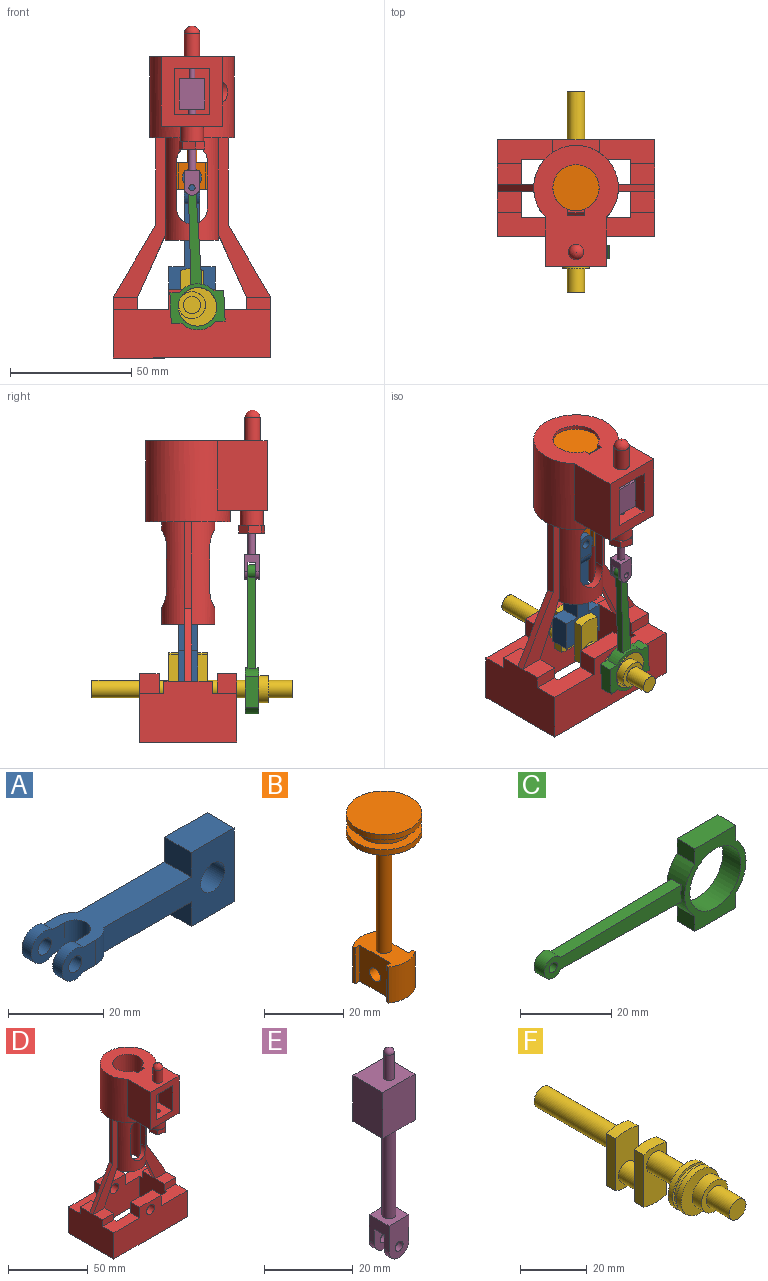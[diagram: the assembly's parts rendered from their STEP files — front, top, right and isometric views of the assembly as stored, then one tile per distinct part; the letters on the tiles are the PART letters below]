
ASSEMBLY  parts=6 mates=7
PART A: 21 faces, bbox 53.2x11.9x19.1 mm
  f0: plane 12.7x7.94mm, normal (0,0,1), area 100.8mm2, adj f1,f2,f13,f15
  f1: plane 19.05x7.94mm, normal (1,0,0), area 151.2mm2, adj f0,f8,f13,f15
  f2: plane 7.94x6.35mm, normal (-1,0,0), area 50.4mm2, adj f0,f3,f13,f15
  f3: plane 34.13x11.91mm, normal (0,0,1), area 258.6mm2, adj f2,f4,f5,f10,f11,f13,f14,f15
  f4: cylinder r=3.97mm len=7.94mm, axis (0,-1,0), area 48.8mm2, adj f3,f6,f11,f18
  f5: cylinder r=3.97mm len=7.94mm, axis (0,-1,0), area 48.8mm2, adj f3,f6,f10,f19
  f6: plane 34.13x11.91mm, normal (0,0,-1), area 258.6mm2, adj f4,f5,f7,f10,f11,f13,f14,f15
  f7: plane 7.94x6.35mm, normal (-1,0,0), area 50.4mm2, adj f6,f8,f13,f15
  f8: plane 12.7x7.94mm, normal (0,0,-1), area 100.8mm2, adj f1,f7,f13,f15
  f9: cylinder r=1.98mm len=3.97mm, axis (0,-1,0), area 34.6mm2, adj f11,f18
  f10: plane 10x7.94mm, normal (0,1,0), area 53.2mm2, adj f3,f5,f6,f12,f16
  f11: plane 10x7.94mm, normal (0,-1,0), area 53.2mm2, adj f3,f4,f6,f9,f14
  f12: cylinder r=1.98mm len=3.97mm, axis (0,-1,0), area 34.6mm2, adj f10,f19
  f13: plane 38.74x19.05mm, normal (0,-1,0), area 367.2mm2, adj f0,f1,f2,f3,f6,f7,f8,f14
  f14: cylinder r=5.95mm len=6.35mm, axis (0,0,1), area 31.8mm2, adj f3,f6,f11,f13
  f15: plane 38.74x19.05mm, normal (0,1,0), area 367.2mm2, adj f0,f1,f2,f3,f6,f7,f8,f16
  f16: cylinder r=5.95mm len=6.35mm, axis (0,0,1), area 31.8mm2, adj f3,f6,f10,f15
  f17: cylinder r=3.17mm len=6.35mm, axis (0,0,1), area 63.3mm2, adj f3,f6,f18,f19
  f18: plane 10x7.94mm, normal (0,1,0), area 53.2mm2, adj f3,f4,f6,f9,f17
  f19: plane 10x7.94mm, normal (0,-1,0), area 53.2mm2, adj f3,f5,f6,f12,f17
  f20: cylinder r=3.57mm len=7.94mm, axis (0,-1,0), area 178.1mm2, adj f13,f15
PART B: 23 faces, bbox 19.1x19.1x53.2 mm
  f0: cylinder r=9.53mm len=19.05mm, axis (0,0,1), area 100.2mm2, adj f1,f7
  f1: plane 19.05x19.05mm, normal (0,0,1), area 285mm2, adj f0
  f2: cylinder r=1.98mm len=35.72mm, axis (0,0,1), area 445.3mm2, adj f3,f21
  f3: plane 19.05x19.05mm, normal (0,0,-1), area 272.7mm2, adj f2,f4
  f4: cylinder r=9.53mm len=19.05mm, axis (0,0,1), area 100.2mm2, adj f3,f5
  f5: plane 19.05x19.05mm, normal (0,0,1), area 131.1mm2, adj f4,f6
  f6: cylinder r=7mm len=14mm, axis (0,0,1), area 131.9mm2, adj f5,f7
  f7: plane 19.05x19.05mm, normal (0,0,-1), area 131.1mm2, adj f0,f6
  f8: plane 11.11x0.85mm, normal (-1,0,0), area 9.4mm2, adj f9,f19,f20,f21
  f9: cylinder r=7.94mm len=11.11mm, axis (0,0,1), area 113.5mm2, adj f8,f10,f20,f21
  f10: plane 11.11x0.85mm, normal (1,0,0), area 9.4mm2, adj f9,f11,f20,f21
  f11: plane 11.11x1.59mm, normal (0,-1,0), area 17.6mm2, adj f10,f12,f20,f21
  f12: plane 11.11x11mm, normal (1,0,0), area 109.9mm2, adj f11,f13,f20,f21,f22
  f13: plane 11.11x1.59mm, normal (0,1,0), area 17.6mm2, adj f12,f14,f20,f21
  f14: plane 11.11x0.85mm, normal (1,0,0), area 9.4mm2, adj f13,f15,f20,f21
  f15: cylinder r=7.94mm len=11.11mm, axis (0,0,1), area 113.5mm2, adj f14,f16,f20,f21
  f16: plane 11.11x0.85mm, normal (-1,0,0), area 9.4mm2, adj f15,f17,f20,f21
  f17: plane 11.11x1.59mm, normal (0,1,0), area 17.6mm2, adj f16,f18,f20,f21
  f18: plane 11.11x11mm, normal (-1,0,0), area 109.9mm2, adj f17,f19,f20,f21,f22
  f19: plane 11.11x1.59mm, normal (0,-1,0), area 17.6mm2, adj f8,f18,f20,f21
  f20: plane 15.88x9.53mm, normal (0,0,-1), area 106.6mm2, adj f8,f9,f10,f11,f12,f13,f14,f15
  f21: plane 15.88x9.53mm, normal (0,0,1), area 94.3mm2, adj f2,f8,f9,f10,f11,f12,f13,f14
  f22: cylinder r=1.98mm len=6.35mm, axis (1,0,0), area 79.2mm2, adj f12,f18
PART C: 17 faces, bbox 61.5x5.6x22.2 mm
  f0: plane 37.68x3.18mm, normal (-0.02,0,1), area 119.6mm2, adj f1,f6,f15,f16
  f1: cylinder r=2.78mm len=5.56mm, axis (0,-1,0), area 44.7mm2, adj f0,f2,f15,f16
  f2: plane 37.68x3.18mm, normal (-0.02,0,-1), area 119.6mm2, adj f1,f6,f15,f16
  f3: cylinder r=1.27mm len=3.18mm, axis (0,-1,0), area 25.3mm2, adj f15,f16
  f4: plane 22.23x19.05mm, normal (0,1,0), area 146.8mm2, adj f6,f7,f8,f9,f10,f11,f12,f13
  f5: plane 22.23x19.05mm, normal (0,-1,0), area 146.8mm2, adj f6,f7,f8,f9,f10,f11,f12,f13
  f6: cylinder r=9.53mm len=14.2mm, axis (0,-1,0), area 74.6mm2, adj f0,f2,f4,f5,f7,f13,f15,f16
  f7: plane 5.56x4.01mm, normal (-1,0,0), area 22.3mm2, adj f4,f5,f6,f8
  f8: plane 12.7x5.56mm, normal (0,0,-1), area 70.6mm2, adj f4,f5,f7,f9
  f9: plane 5.56x4.01mm, normal (1,0,0), area 22.3mm2, adj f4,f5,f8,f10
  f10: cylinder r=9.53mm len=14.2mm, axis (0,-1,0), area 89mm2, adj f4,f5,f9,f11
  f11: plane 5.56x4.01mm, normal (1,0,0), area 22.3mm2, adj f4,f5,f10,f12
  f12: plane 12.7x5.56mm, normal (0,0,1), area 70.6mm2, adj f4,f5,f11,f13
  f13: plane 5.56x4.01mm, normal (-1,0,0), area 22.3mm2, adj f4,f5,f6,f12
  f14: cylinder r=7.94mm len=15.88mm, axis (0,-1,0), area 277.1mm2, adj f4,f5
  f15: plane 42.73x5.56mm, normal (0,-1,0), area 161.7mm2, adj f0,f1,f2,f3,f6
  f16: plane 42.73x5.56mm, normal (0,1,0), area 161.7mm2, adj f0,f1,f2,f3,f6
PART D: 127 faces, bbox 65x52.5x136.9 mm
  f0: plane 2.38x1.37mm, normal (0,0,1), area 0.8mm2, adj f104,f108
  f1: cylinder r=17.46mm len=34.93mm, axis (0,0,1), area 2826.3mm2, adj f13,f72,f73,f74,f75,f98
  f2: plane 19.05x18.38mm, normal (0,0,1), area 263.1mm2, adj f4,f50,f86,f90,f91
  f3: plane 19.05x14.29mm, normal (0,-1,0), area 222.2mm2, adj f77,f78,f81,f82,f83,f89,f90,f91
  f4: cylinder r=9.53mm len=27.78mm, axis (0,0,-1), area 1642.9mm2, adj f2,f74,f80,f81,f82,f87,f90,f91
  f5: plane 25.78x11.6mm, normal (0.91,0,-0.41), area 84.3mm2, adj f6,f7,f12,f23
  f6: plane 65.88x21.6mm, normal (0,-1,0), area 377.6mm2, adj f5,f12,f13,f31,f39,f45,f46
  f7: plane 65.88x21.6mm, normal (0,1,0), area 377.6mm2, adj f5,f12,f13,f15,f39,f45,f46
  f8: plane 25.78x11.6mm, normal (-0.91,0,-0.41), area 84.3mm2, adj f9,f10,f25,f59
  f9: plane 65.88x21.6mm, normal (0,-1,0), area 377.6mm2, adj f8,f12,f13,f36,f40,f47,f48
  f10: plane 65.88x21.6mm, normal (0,1,0), area 377.6mm2, adj f8,f12,f13,f14,f40,f47,f48
  f11: cylinder r=7.94mm len=41.56mm, axis (0,0,1), area 1209.9mm2, adj f49,f51,f52,f53,f54,f55,f56,f57
  f12: cylinder r=11mm len=42.38mm, axis (0,0,1), area 1880mm2, adj f5,f6,f7,f9,f10,f13,f51,f52
  f13: plane 34.93x34.93mm, normal (0,0,-1), area 554.3mm2, adj f1,f6,f7,f9,f10,f12,f46,f47
  f14: plane 10x8.5mm, normal (0,0,1), area 85mm2, adj f10,f25,f27,f34
  f15: plane 10x8.5mm, normal (0,0,1), area 85mm2, adj f7,f21,f23,f29
  f16: plane 23x10mm, normal (0,0,1), area 204mm2, adj f22,f25,f26,f27,f35,f37
  f17: plane 23x10mm, normal (0,0,1), area 204mm2, adj f20,f24,f25,f27,f33,f34
  f18: plane 23x10mm, normal (0,0,1), area 204mm2, adj f21,f22,f23,f26,f30,f38
  f19: plane 23x10mm, normal (0,0,1), area 204mm2, adj f20,f21,f23,f24,f29,f32
  f20: plane 65x28.18mm, normal (0,1,0), area 1415.2mm2, adj f17,f19,f21,f27,f28,f32,f33,f41
  f21: plane 40x25mm, normal (-1,0,0), area 900mm2, adj f15,f18,f19,f20,f22,f28,f29,f30
  f22: plane 65x28.18mm, normal (0,-1,0), area 1415.2mm2, adj f16,f18,f21,f27,f28,f37,f38,f42
  f23: plane 25x24mm, normal (1,0,0), area 580mm2, adj f5,f15,f18,f19,f24,f26,f28,f29
  f24: plane 45x28.18mm, normal (0,-1,0), area 1015.2mm2, adj f17,f19,f23,f25,f28,f32,f33,f41
  f25: plane 25x24mm, normal (-1,0,0), area 580mm2, adj f8,f14,f16,f17,f24,f26,f28,f34
  f26: plane 45x28.18mm, normal (0,1,0), area 1015.2mm2, adj f16,f18,f23,f25,f28,f37,f38,f42
  f27: plane 40x25mm, normal (1,0,0), area 900mm2, adj f14,f16,f17,f20,f22,f28,f34,f35
  f28: plane 65x40mm, normal (0,0,-1), area 1520mm2, adj f20,f21,f22,f23,f24,f25,f26,f27
  f29: plane 10x5mm, normal (0,1,0), area 50mm2, adj f15,f19,f21,f23
  f30: plane 10x5mm, normal (0,-1,0), area 50mm2, adj f18,f21,f23,f31
  f31: plane 10x8.5mm, normal (0,0,1), area 85mm2, adj f6,f21,f23,f30
  f32: plane 8.18x8mm, normal (-1,0,0), area 65.4mm2, adj f19,f20,f24,f41
  f33: plane 8.18x8mm, normal (1,0,0), area 65.4mm2, adj f17,f20,f24,f41
  f34: plane 10x5mm, normal (0,1,0), area 50mm2, adj f14,f17,f25,f27
  f35: plane 10x5mm, normal (0,-1,0), area 50mm2, adj f16,f25,f27,f36
  f36: plane 10x8.5mm, normal (0,0,1), area 85mm2, adj f9,f25,f27,f35
  f37: plane 8.18x8mm, normal (1,0,0), area 65.4mm2, adj f16,f22,f26,f42
  f38: plane 8.18x8mm, normal (-1,0,0), area 65.4mm2, adj f18,f22,f26,f42
  f39: plane 30x17.63mm, normal (-0.86,0,0.51), area 104.4mm2, adj f6,f7,f21,f45
  f40: plane 30x17.63mm, normal (0.86,0,0.51), area 104.4mm2, adj f9,f10,f27,f48
  f41: plane 19x8mm, normal (0,0,1), area 152mm2, adj f20,f24,f32,f33
  f42: plane 19x8mm, normal (0,0,1), area 152mm2, adj f22,f26,f37,f38
  f43: cylinder r=3.57mm len=8mm, axis (0,-1,0), area 179.5mm2, adj f22,f26
  f44: cylinder r=3.57mm len=8mm, axis (0,-1,0), area 179.5mm2, adj f20,f24
  f45: plane 3x0.02mm, normal (0,0,-1), area 0.1mm2, adj f6,f7,f39,f46
  f46: plane 35.88x3mm, normal (-1,0,0), area 107.6mm2, adj f6,f7,f13,f45
  f47: plane 35.88x3mm, normal (1,0,0), area 107.6mm2, adj f9,f10,f13,f48
  f48: plane 3x0.02mm, normal (0,0,-1), area 0.1mm2, adj f9,f10,f40,f47
  f49: plane 15.88x15.88mm, normal (0,0,-1), area 148.4mm2, adj f11,f61
  f50: cylinder r=1.98mm len=10.35mm, axis (0,0,-1), area 129mm2, adj f2,f70
  f51: plane 19.75x4.22mm, normal (-1,0,0), area 83.3mm2, adj f11,f12,f52,f54
  f52: cylinder r=6.35mm len=12.7mm, axis (0,1,0), area 71.2mm2, adj f11,f12,f51,f53
  f53: plane 19.75x4.22mm, normal (1,0,0), area 83.3mm2, adj f11,f12,f52,f54
  f54: cylinder r=6.35mm len=12.7mm, axis (0,1,0), area 71.2mm2, adj f11,f12,f51,f53
  f55: cylinder r=6.35mm len=12.7mm, axis (0,1,0), area 71.2mm2, adj f11,f12,f56,f58
  f56: plane 19.75x4.22mm, normal (1,0,0), area 83.3mm2, adj f11,f12,f55,f57
  f57: cylinder r=6.35mm len=12.7mm, axis (0,1,0), area 71.2mm2, adj f11,f12,f56,f58
  f58: plane 19.75x4.22mm, normal (-1,0,0), area 83.3mm2, adj f11,f12,f55,f57
  f59: extruded ~3x2.28mm, area 6.4mm2, adj f8,f12,f60
  f60: plane 22x22mm, normal (0,0,-1), area 182.2mm2, adj f11,f12,f59
  f61: cylinder r=3.97mm len=7.94mm, axis (0,0,1), area 19.9mm2, adj f49,f71
  f62: plane 4.82x3.18mm, normal (-0.4,-0.92,0), area 16.7mm2, adj f63,f69,f70,f71
  f63: plane 4.9x3.18mm, normal (-0.93,-0.37,0), area 16.7mm2, adj f62,f64,f70,f71
  f64: plane 4.82x3.18mm, normal (-0.92,0.4,0), area 16.7mm2, adj f63,f65,f70,f71
  f65: plane 4.9x3.18mm, normal (-0.37,0.93,0), area 16.7mm2, adj f64,f66,f70,f71
  f66: plane 4.82x3.18mm, normal (0.4,0.92,0), area 16.7mm2, adj f65,f67,f70,f71
  f67: plane 4.9x3.18mm, normal (0.93,0.37,0), area 16.7mm2, adj f66,f68,f70,f71
  f68: plane 4.82x3.18mm, normal (0.92,-0.4,0), area 16.7mm2, adj f67,f69,f70,f71
  f69: plane 4.9x3.18mm, normal (0.37,-0.93,0), area 16.7mm2, adj f62,f68,f70,f71
  f70: plane 13.74x13.74mm, normal (0,0,-1), area 121.2mm2, adj f50,f62,f63,f64,f65,f66,f67,f68
  f71: plane 13.74x13.74mm, normal (0,0,1), area 84.1mm2, adj f61,f62,f63,f64,f65,f66,f67,f68
  f72: plane 28.58x23.02mm, normal (1,0,0), area 570.4mm2, adj f1,f74,f75,f96,f98,f103
  f73: plane 28.58x20.56mm, normal (-1,0,0), area 587.5mm2, adj f1,f74,f75,f103
  f74: plane 50.01x34.93mm, normal (0,0,1), area 1052.2mm2, adj f1,f4,f72,f73,f76,f81,f82,f103
  f75: plane 25.4x20.56mm, normal (0,0,-1), area 354.8mm2, adj f1,f72,f73,f103,f113
  f76: plane 8.94x7mm, normal (0,0.9,-0.44), area 69.7mm2, adj f74,f77,f81,f82
  f77: plane 7x4mm, normal (0,0,-1), area 28mm2, adj f3,f76,f81,f82
  f78: plane 7x5.24mm, normal (0,0,1), area 36.7mm2, adj f3,f79,f81,f82
  f79: plane 8.94x7mm, normal (0,-0.9,0.44), area 69.7mm2, adj f78,f80,f81,f82
  f80: plane 7x1.38mm, normal (0,0,1), area 6.5mm2, adj f4,f79,f81,f82
  f81: plane 10.99x10.93mm, normal (1,0,0), area 32.9mm2, adj f3,f4,f74,f76,f77,f78,f79,f80
  f82: plane 10.99x10.93mm, normal (-1,0,0), area 32.9mm2, adj f3,f4,f74,f76,f77,f78,f79,f80
  f83: plane 7x4mm, normal (0,0,1), area 28mm2, adj f3,f84,f90,f91
  f84: plane 8.94x7mm, normal (0,0.9,0.44), area 69.7mm2, adj f83,f85,f90,f91
  f85: plane 7x3.54mm, normal (0,0,1), area 24.8mm2, adj f84,f86,f90,f91
  f86: plane 7x1.22mm, normal (0,-1,0), area 8.5mm2, adj f2,f85,f90,f91
  f87: plane 7x1.38mm, normal (0,0,-1), area 6.5mm2, adj f4,f88,f90,f91
  f88: plane 8.94x7mm, normal (0,-0.9,-0.44), area 69.7mm2, adj f87,f89,f90,f91
  f89: plane 7x5.24mm, normal (0,0,-1), area 36.7mm2, adj f3,f88,f90,f91
  f90: plane 11.91x10.93mm, normal (1,0,0), area 34mm2, adj f2,f3,f4,f83,f84,f85,f86,f87
  f91: plane 11.91x10.93mm, normal (-1,0,0), area 34mm2, adj f2,f3,f4,f83,f84,f85,f86,f87
  f92: plane 7x2.81mm, normal (0,0,-1), area 19.6mm2, adj f3,f94,f95,f96
  f93: plane 7x2.81mm, normal (0,0,1), area 19.6mm2, adj f3,f94,f95,f96
  f94: plane 3.18x2.81mm, normal (1,0,0), area 8mm2, adj f3,f92,f93,f96
  f95: plane 3.18x2.81mm, normal (-1,0,0), area 8mm2, adj f3,f92,f93,f96
  f96: cylinder r=3.17mm len=18mm, axis (1,0,0), area 335.8mm2, adj f72,f92,f93,f94,f95,f97
  f97: plane 6.35x6.35mm, normal (1,0,0), area 31.7mm2, adj f96
  f98: cylinder r=4.76mm len=8.34mm, axis (-1,0,0), area 13.3mm2, adj f1,f72
  f99: plane 19.05x12.7mm, normal (1,0,0), area 241.9mm2, adj f3,f100,f102,f103
  f100: plane 14.29x12.7mm, normal (0,0,-1), area 177mm2, adj f3,f99,f101,f103,f104
  f101: plane 19.05x12.7mm, normal (-1,0,0), area 241.9mm2, adj f3,f100,f102,f103
  f102: plane 14.29x12.7mm, normal (0,0,1), area 173.5mm2, adj f3,f99,f101,f103,f110
  f103: plane 28.58x25.4mm, normal (0,-1,0), area 453.6mm2, adj f72,f73,f74,f75,f99,f100,f101,f102
  f104: cylinder r=1.19mm len=4.76mm, axis (0,0,1), area 35.6mm2, adj f0,f100,f107
  f105: sphere r=3.17mm, area 59.8mm2, adj f106
  f106: cylinder r=3.17mm len=9.7mm, axis (0,0,1), area 193.2mm2, adj f74,f105
  f107: plane 2.38x1.37mm, normal (0,0,-1), area 0.8mm2, adj f104,f108
  f108: cylinder r=1.19mm len=8.73mm, axis (0,0,1), area 65.3mm2, adj f0,f107,f109
  f109: plane 2.38x2.38mm, normal (0,0,-1), area 4.5mm2, adj f108
  f110: cylinder r=1.59mm len=4.76mm, axis (0,0,-1), area 47.6mm2, adj f102,f111
  f111: plane 3.18x3.18mm, normal (0,0,1), area 0mm2, adj f110,f112
  f112: cylinder r=1.59mm len=9.53mm, axis (0,0,1), area 95mm2, adj f111,f126
  f113: cylinder r=4.76mm len=9.53mm, axis (0,0,1), area 190mm2, adj f75,f114,f115,f116,f117,f118,f119
  f114: plane 4.6x1.94mm, normal (0,0,1), area 1.2mm2, adj f113,f122,f123
  f115: plane 3.37x3.37mm, normal (0,0,1), area 1.2mm2, adj f113,f123,f124
  f116: plane 4.6x1.94mm, normal (0,0,1), area 1.2mm2, adj f113,f124,f125
  f117: plane 4.6x1.94mm, normal (0,0,1), area 1.2mm2, adj f113,f120,f125
  f118: plane 3.37x3.37mm, normal (0,0,1), area 1.2mm2, adj f113,f120,f121
  f119: plane 4.6x1.94mm, normal (0,0,1), area 1.2mm2, adj f113,f121,f122
  f120: plane 5.31x3.18mm, normal (-0.26,-0.97,0), area 17.5mm2, adj f117,f118,f121,f125,f126
  f121: plane 5.31x3.18mm, normal (-0.97,-0.26,0), area 17.5mm2, adj f118,f119,f120,f122,f126
  f122: plane 3.89x3.89mm, normal (-0.71,0.71,0), area 17.5mm2, adj f114,f119,f121,f123,f126
  f123: plane 5.31x3.18mm, normal (0.26,0.97,0), area 17.5mm2, adj f114,f115,f122,f124,f126
  f124: plane 5.31x3.18mm, normal (0.97,0.26,0), area 17.5mm2, adj f115,f116,f123,f125,f126
  f125: plane 3.89x3.89mm, normal (0.71,-0.71,0), area 17.5mm2, adj f116,f117,f120,f124,f126
  f126: plane 10.62x10.62mm, normal (0,0,-1), area 70.7mm2, adj f112,f120,f121,f122,f123,f124,f125
PART E: 26 faces, bbox 10.3x9.6x56.4 mm
  f0: plane 12.7x10.32mm, normal (0,1,0), area 80mm2, adj f14,f16,f17,f18,f21,f22,f23,f24
  f1: cylinder r=1.59mm len=25.2mm, axis (0,0,-1), area 251.3mm2, adj f8,f17
  f2: plane 7.14x6.35mm, normal (-1,0,0), area 32.8mm2, adj f3,f5,f8,f9,f10,f11,f12,f13
  f3: cylinder r=3.17mm len=6.35mm, axis (0,-1,0), area 15.8mm2, adj f2,f6,f9,f12
  f4: cylinder r=1.27mm len=2.54mm, axis (0,-1,0), area 12.7mm2, adj f9,f12
  f5: cylinder r=3.17mm len=6.35mm, axis (0,-1,0), area 15.8mm2, adj f2,f6,f10,f13
  f6: plane 7.14x6.35mm, normal (1,0,0), area 32.8mm2, adj f3,f5,f8,f9,f10,f11,f12,f13
  f7: cylinder r=1.27mm len=2.54mm, axis (0,-1,0), area 12.7mm2, adj f10,f13
  f8: plane 6.35x6.35mm, normal (0,0,1), area 32.4mm2, adj f1,f2,f6,f9,f10
  f9: plane 10.32x6.35mm, normal (0,1,0), area 56.1mm2, adj f2,f3,f4,f6,f8
  f10: plane 10.32x6.35mm, normal (0,-1,0), area 56.1mm2, adj f2,f5,f6,f7,f8
  f11: plane 6.35x3.18mm, normal (0,0,-1), area 20.2mm2, adj f2,f6,f12,f13
  f12: plane 7.14x6.35mm, normal (0,-1,0), area 36mm2, adj f2,f3,f4,f6,f11
  f13: plane 7.14x6.35mm, normal (0,1,0), area 36mm2, adj f2,f5,f6,f7,f11
  f14: plane 12.7x9.53mm, normal (-1,0,0), area 121mm2, adj f0,f15,f17,f18
  f15: plane 12.7x10.32mm, normal (0,-1,0), area 131mm2, adj f14,f16,f17,f18
  f16: plane 12.7x9.53mm, normal (1,0,0), area 121mm2, adj f0,f15,f17,f18
  f17: plane 10.32x9.53mm, normal (0,0,-1), area 90.4mm2, adj f0,f1,f14,f15,f16
  f18: plane 10.32x9.53mm, normal (0,0,1), area 93.8mm2, adj f0,f14,f15,f16,f20
  f19: sphere r=1.19mm, area 8.9mm2, adj f20
  f20: cylinder r=1.19mm len=7.03mm, axis (0,0,-1), area 52.6mm2, adj f18,f19
  f21: plane 7.14x0.79mm, normal (0,0,-1), area 5.7mm2, adj f0,f22,f24,f25
  f22: plane 7.14x0.79mm, normal (-1,0,0), area 5.7mm2, adj f0,f21,f23,f25
  f23: plane 7.14x0.79mm, normal (0,0,1), area 5.7mm2, adj f0,f22,f24,f25
  f24: plane 7.14x0.79mm, normal (1,0,0), area 5.7mm2, adj f0,f21,f23,f25
  f25: plane 7.14x7.14mm, normal (0,1,0), area 51mm2, adj f21,f22,f23,f24
PART F: 27 faces, bbox 15.9x82.6x23.8 mm
  f0: cylinder r=3.57mm len=15.7mm, axis (0,1,0), area 352.3mm2, adj f6,f17
  f1: plane 19.09x3.97mm, normal (1,0,0), area 75.8mm2, adj f2,f4,f5,f6
  f2: cylinder r=15.08mm len=9.53mm, axis (0,-1,0), area 38.5mm2, adj f1,f3,f5,f6
  f3: plane 19.09x3.97mm, normal (-1,0,0), area 75.8mm2, adj f2,f4,f5,f6
  f4: cylinder r=15.08mm len=9.53mm, axis (0,-1,0), area 38.5mm2, adj f1,f3,f5,f6
  f5: plane 20.64x9.53mm, normal (0,1,0), area 151.6mm2, adj f1,f2,f3,f4,f7
  f6: plane 20.64x9.53mm, normal (0,-1,0), area 151.6mm2, adj f0,f1,f2,f3,f4
  f7: cylinder r=3.57mm len=7.94mm, axis (0,-1,0), area 178.1mm2, adj f5,f13
  f8: cylinder r=15.08mm len=9.53mm, axis (0,-1,0), area 38.5mm2, adj f9,f11,f12,f13
  f9: plane 19.09x3.97mm, normal (1,0,0), area 75.8mm2, adj f8,f10,f12,f13
  f10: cylinder r=15.08mm len=9.53mm, axis (0,-1,0), area 38.5mm2, adj f9,f11,f12,f13
  f11: plane 19.09x3.97mm, normal (-1,0,0), area 75.8mm2, adj f8,f10,f12,f13
  f12: plane 20.64x9.53mm, normal (0,1,0), area 151.6mm2, adj f8,f9,f10,f11,f14
  f13: plane 20.64x9.53mm, normal (0,-1,0), area 151.6mm2, adj f7,f8,f9,f10,f11
  f14: cylinder r=3.57mm len=31.75mm, axis (0,-1,0), area 712.6mm2, adj f12,f15
  f15: plane 7.14x7.14mm, normal (0,1,0), area 40.1mm2, adj f14
  f16: cylinder r=7.94mm len=15.88mm, axis (0,-1,0), area 99mm2, adj f17,f18
  f17: plane 15.88x15.88mm, normal (0,1,0), area 157.9mm2, adj f0,f16
  f18: plane 15.88x15.88mm, normal (0,-1,0), area 37.6mm2, adj f16,f26
  f19: plane 7.14x7.14mm, normal (0,-1,0), area 40.1mm2, adj f20
  f20: cylinder r=3.57mm len=9.7mm, axis (0,1,0), area 217.8mm2, adj f19,f21
  f21: plane 11.11x11.11mm, normal (0,-1,0), area 56.9mm2, adj f20,f22
  f22: cylinder r=5.56mm len=11.11mm, axis (0,-1,0), area 138.6mm2, adj f21,f23
  f23: plane 15.88x15.88mm, normal (0,-1,0), area 100.9mm2, adj f22,f24
  f24: cylinder r=7.94mm len=15.88mm, axis (0,-1,0), area 99mm2, adj f23,f25
  f25: plane 15.88x15.88mm, normal (0,1,0), area 37.6mm2, adj f24,f26
  f26: cylinder r=7.14mm len=14.29mm, axis (0,-1,0), area 71.3mm2, adj f18,f25
PLACE A rot(axis=(0,1,0),90deg) t=(0,14.05,9.53)mm
PLACE B rot(axis=(0,0,-1),90deg) t=(0,20,58.74)mm
PLACE C rot(axis=(0,1,0),87.4deg) t=(2.26,-9.02,-0.74)mm
PLACE D t=(0,20,-21.83)mm
PLACE E rot(axis=(0,0.03,1),0deg) t=(0,-9.42,48.42)mm
PLACE F rot(axis=(0,-1,0),180deg) t=(0,12.06,4.76)mm
MATE revolute E.f4 <-> C.f3  axis (0,1,0) through (0,-7.83,48.42)mm
MATE revolute A.f20 <-> F.f7  axis (0,-1,0) through (0,16.03,9.53)mm
MATE cylindrical D.f104 <-> E.f1  axis (0,0,1) through (0,-6.19,78.58)mm
MATE revolute A.f9 <-> B.f22  axis (0,-1,0) through (0,23.18,52.39)mm
MATE cylindrical B.f0 <-> D.f4  axis (0,0,1) through (0,20,100.81)mm
MATE cylindrical C.f14 <-> F.f16  axis (0,-1,0) through (2.26,-9.02,-0.74)mm
MATE cylindrical D.f43 <-> F.f0  axis (0,-1,0) through (0,0,0)mm
